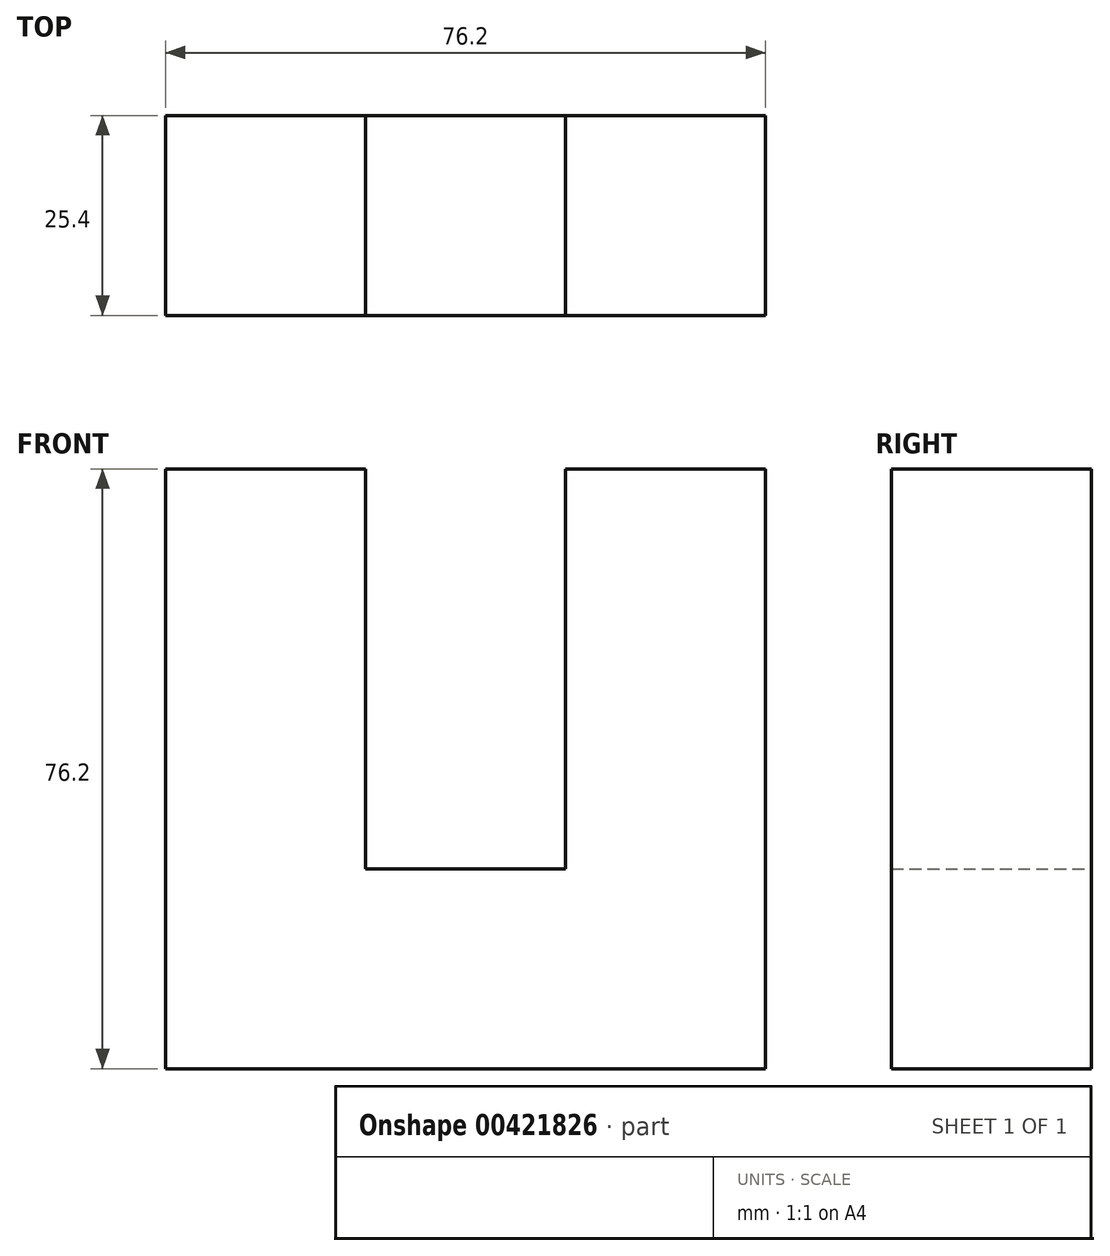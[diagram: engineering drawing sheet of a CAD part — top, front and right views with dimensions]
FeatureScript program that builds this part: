
annotation { "Feature Type Name" : "Feature", "Feature Type Description" : "" }
export const myFeature = defineFeature(function(context is Context, id is Id, definition is map)
    precondition{}
    {
        {
            var Q0;
            Q0=qCreatedBy(makeId("Front.planeOp"),FACE);
            var sketch = newSketch(context, id + "F0", { "sketchPlane" : qUnion([Q0])});
            skLineSegment(sketch, "E0", {"start": v(0, 0) * mm, "end": v(-76.2, 0) * mm});
            skLineSegment(sketch, "E1", {"start": v(-76.2, 0) * mm, "end": v(-76.2, 76.2) * mm});
            skLineSegment(sketch, "E2", {"start": v(-76.2, 76.2) * mm, "end": v(-50.8, 76.2) * mm});
            skLineSegment(sketch, "E3", {"start": v(-50.8, 76.2) * mm, "end": v(-50.8, 25.4) * mm});
            skLineSegment(sketch, "E4", {"start": v(-50.8, 25.4) * mm, "end": v(-25.4, 25.4) * mm});
            skLineSegment(sketch, "E5", {"start": v(-25.4, 25.4) * mm, "end": v(-25.4, 76.2) * mm});
            skLineSegment(sketch, "E6", {"start": v(-25.4, 76.2) * mm, "end": v(0, 76.2) * mm});
            skLineSegment(sketch, "E7", {"start": v(0, 0) * mm, "end": v(0, 76.2) * mm});
            skSolve(sketch);
        }
        {
            var Q0;
            Q0 = qSketchRegion(id + "F0", true);
            extrude(context, id + "F1", {"entities" : qUnion([Q0]), "depth" : 25.4 * mm});
        }
    });
